MODEL slx_f605d08cfd22
CONFIG AbsTol = auto
CONFIG FixedStep = 0.01
CONFIG MaxStep = auto
CONFIG MinStep = auto
CONFIG RelTol = 1e-3
CONFIG SampleTimeConstraint = Unconstrained
CONFIG Solver = FixedStepDiscrete
CONFIG SolverMode = Auto
CONFIG SolverName = FixedStepDiscrete
CONFIG StartTime = 0.0
CONFIG StopTime = 10.0
BLOCK [Reference] Compare To Zero  REF=simulink/Logic and Bit
Operations/Compare
To Zero
  Ports = [1, 1]
  SourceBlock = simulink/Logic and Bit
Operations/Compare
To Zero
  SourceType = Compare To Zero
BLOCK [Constant] Constant
  Value = 0
BLOCK [Constant] Constant1
  SampleTime = 0
  Value = 200
BLOCK [Constant] Constant2
  SampleTime = 0
BLOCK [RelationalOperator] Relational Operator
  InputSameDT = off
  Operator = <=
  OutDataTypeStr = boolean
  Ports = [2, 1]
BLOCK [Scope] Scope
  NumInputPorts = 3
  Ports = [3]
  ScopeSpecificationString = Simulink.scopes.TimeScopeBlockCfg('CurrentConfiguration', extmgr.ConfigurationSet(extmgr.Configuration('Core','General UI',true),extmgr.Configuration('Core','Source UI',true),extmgr.Configuration('Sources','WiredSimulink',true,'DataLoggingSaveFormat','StructureWithTime','DataLoggingLimitDataPoints',true,'DataLoggingDecimation','1','DataLoggingDecimateData',true),extmgr.Configuration('Visuals','Tim...<+3039ch>
BLOCK [Scope] Scope1
  IOType = viewer
  Ports = []
  ScopeSpecificationString = C++SS(StrPVP('Location','[188, 365, 512, 604]'),StrPVP('Open','off'),MxPVP('AxesTitles',24,'struct(''axes1'',''%<SignalLabel>'')'),StrPVP('ShowDataMarkers','off'),StrPVP('ShowLegends','off'),StrPVP('MaxDataPoints','7500'),StrPVP('LimitDataPoints','on'),StrPVP('DataFormat','Array'),StrPVP('Decimation','1'),StrPVP('BlockParamSampleInput','off'))
BLOCK [Scope] Scope2
  IOType = viewer
  Ports = []
  ScopeSpecificationString = C++SS(StrPVP('Location','[128, 476, 452, 737]'),StrPVP('Open','off'),MxPVP('AxesTitles',24,'struct(''axes1'',''%<SignalLabel>'')'),StrPVP('ShowDataMarkers','off'),StrPVP('ShowLegends','off'),StrPVP('SaveName','ScopeData1'),StrPVP('MaxDataPoints','7500'),StrPVP('LimitDataPoints','on'),StrPVP('DataFormat','Array'),StrPVP('Decimation','1'),StrPVP('BlockParamSampleInput','off'))
BLOCK [SubSystem] Signal Builder
  ClipboardFcn = sigbuilder_block('clipboard');
  CloseFcn = sigbuilder_block('close');
  ContinueFcn = sigbuilder_block('continue');
  CopyFcn = sigbuilder_block('copy');
  DeleteFcn = sigbuilder_block('delete');
  LoadFcn = sigbuilder_block('load');
  MaskHideContents = on
  ModelCloseFcn = sigbuilder_block('modelClose');
  NameChangeFcn = sigbuilder_block('namechange');
  OpenFcn = sigbuilder_block('open',[462 109.5 550.5 393 ]);
  PauseFcn = sigbuilder_block('pause');
  Ports = [0, 1]
  PreSaveFcn = sigbuilder_block('preSave');
  RequestExecContextInheritance = off
  StartFcn = sigbuilder_block('start');
  StopFcn = sigbuilder_block('stop');
  Tag = STV Subsys
  Variant = off
BLOCK [Demux] Signal Builder/Demux
  Outputs = 1
  Ports = [1, 1]
  Tag = STV Demux
BLOCK [FromWorkspace] Signal Builder/FromWs
  SampleTime = 0
  Tag = STV FromWs
  VariableName = tuvar
  ZeroCross = on
BLOCK [Outport] Signal Builder/Signal 1
  IconDisplay = Port number
  Tag = STV Outport
BLOCK [Sum] Subtract
  InputSameDT = off
  Inputs = +-
  OutDataTypeStr = uint16
  Ports = [2, 1]
  RndMeth = Zero
BLOCK [Switch] Switch
  Criteria = u2 ~= 0
  InputSameDT = off
  RndMeth = Ceiling
  SampleTime = 0
  SaturateOnIntegerOverflow = off
BLOCK [UnitDelay] Unit Delay
  SampleTime = -1
LINE Compare To Zero:1 -> Scope:3
LINE Constant1:1 -> Switch:3
LINE Constant2:1 -> Subtract:2
LINE Constant:1 -> Relational Operator:2
LINE Relational Operator:1 -> Switch:2
LINE Signal Builder:1 -> Relational Operator:1
LINE Signal Builder:1 -> Scope:1
LINE Subtract:1 -> Switch:1
LINE Switch:1 -> Compare To Zero:1
LINE Switch:1 -> Scope:2
LINE Switch:1 -> Unit Delay:1
LINE Unit Delay:1 -> Subtract:1
